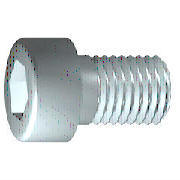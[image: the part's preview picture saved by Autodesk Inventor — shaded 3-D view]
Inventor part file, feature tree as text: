
AUTODESK INVENTOR PART (.ipt)
format: ipt  version: 2022 (Build 260153000, 153)  size: 194,560 bytes
history: native  units: mm (DEFAULTED — no unit token found)
features: sketch x2, extrude x1, plane x1, fillet x1
ambient origin geometry x7: Origin, YZ Plane, XY Plane, X Axis, Y Axis, Z Axis, Center Point
bodies: Solid1 (feature_tree), Body (feature_tree)
feature tree (5):
  extrude  "Slot"  Depth=3.0mm
  plane  "Work Plane1"
  fillet  "Fillet2"  Radius=3.0mm
  sketch  "Sketch1"  dims[d1=8.75mm d2=0.306825mm d3=3.0mm]
  sketch  "Sketch2"  dims[d4=1.3mm d5=60.0deg d6=3.0mm d7=3.0mm d8=2.886751mm d9=5.5mm d10=90.0deg d11=10.0mm d12=0.0mm d13=8.75mm d14=0.0mm d15=0.306725mm d16=0.306725mm d17=0.3mm d19=0.0mm d26=10.0mm d27=45.0deg d28=0.0mm d29=0.0mm d30=0.1mm]
